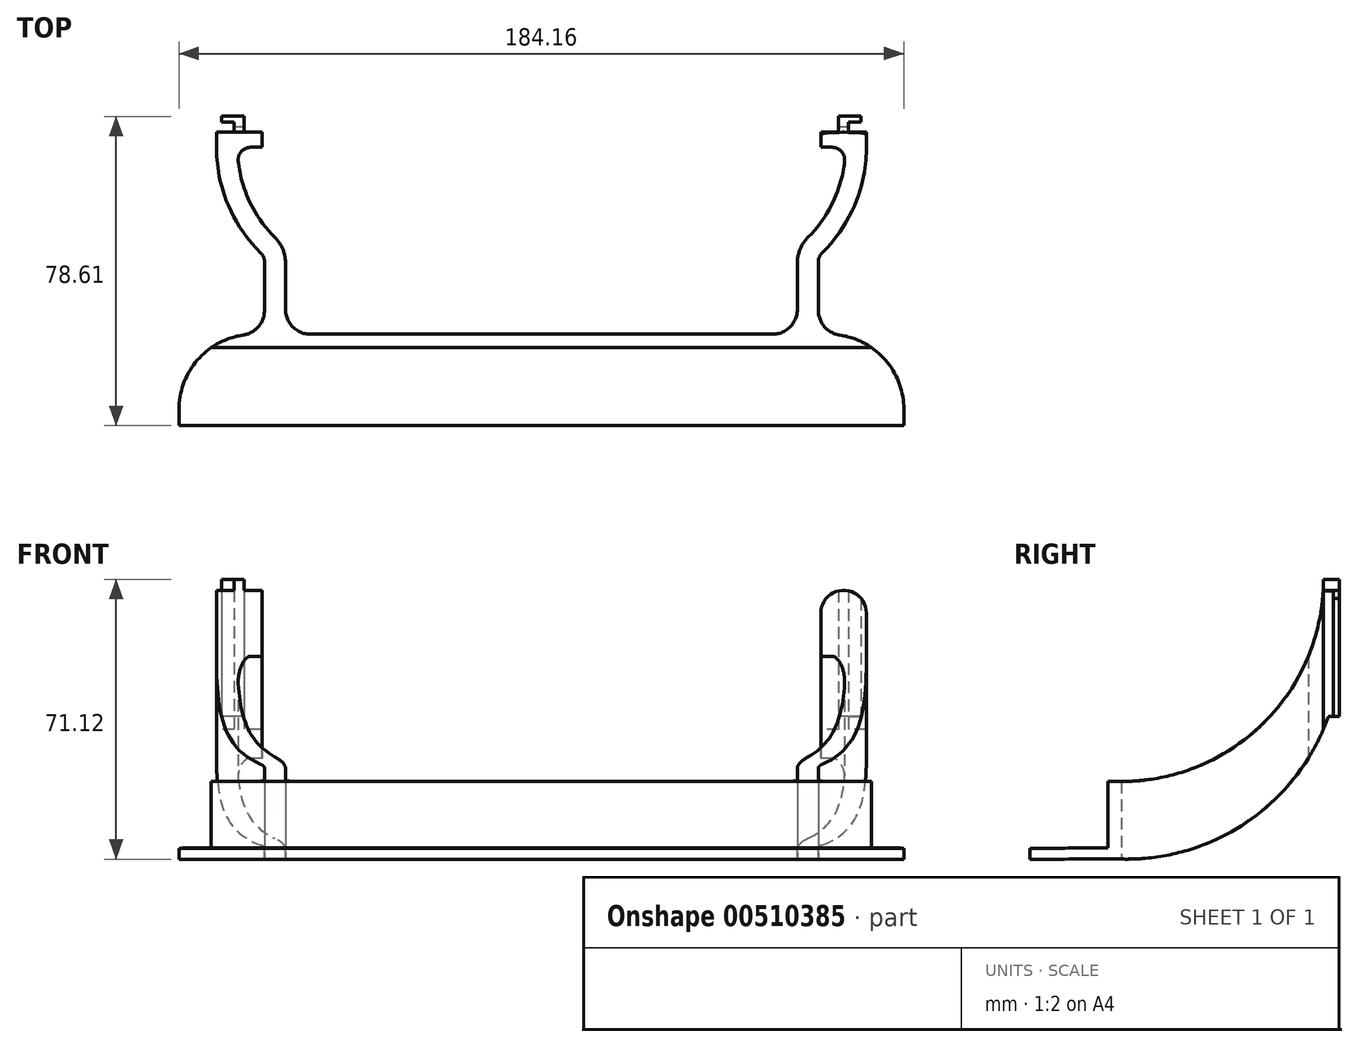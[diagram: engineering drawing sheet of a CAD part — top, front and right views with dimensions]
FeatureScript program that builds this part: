
annotation { "Feature Type Name" : "Feature", "Feature Type Description" : "" }
export const myFeature = defineFeature(function(context is Context, id is Id, definition is map)
    precondition{}
    {
        {
            var Q0;
            Q0=qCreatedBy(makeId("Top.planeOp"),FACE);
            var sketch = newSketch(context, id + "F0", { "sketchPlane" : qUnion([Q0])});
            skLineSegment(sketch, "E0", {"start": v(0, 0) * mm, "end": v(92.07, 0) * mm});
            skLineSegment(sketch, "E1.0", {"start": v(0, 23.24) * mm, "end": v(58.67, 23.24) * mm});
            skLineSegment(sketch, "E2", {"start": v(70.36, 41.66) * mm, "end": v(70.36, 29.32) * mm});
            skLineSegment(sketch, "E3.0", {"start": v(65.02, 41.35) * mm, "end": v(65.02, 29.6) * mm});
            skLineSegment(sketch, "E4", {"start": v(92.07, 0) * mm, "end": v(92.07, 4.2) * mm});
            skPoint(sketch, "E5.visualSharp", {"position": v(92.07, 23.24) * mm});
            skArc(sketch, "E5.filletArc", {"start": v(92.07, 4.2) * mm, "mid": v(87.44, 16.65) * mm, "end": v(75.79, 23.04) * mm});
            skLineSegment(sketch, "E6", {"start": v(82.55, 74.55) * mm, "end": v(82.55, 70.74) * mm});
            skArc(sketch, "E7.trimOffspring", {"start": v(71.3, 43.93) * mm, "mid": v(79.63, 56.2) * mm, "end": v(82.55, 70.74) * mm});
            skArc(sketch, "E8.0", {"start": v(67.75, 47.9) * mm, "mid": v(74.03, 56.77) * mm, "end": v(77.02, 67.22) * mm});
            skLineSegment(sketch, "E9.0", {"start": v(71, 74.55) * mm, "end": v(71, 70.74) * mm});
            skLineSegment(sketch, "E10.trimOffspring", {"start": v(71, 74.55) * mm, "end": v(75.5, 74.55) * mm});
            skLineSegment(sketch, "E11.trimOffspring", {"start": v(71, 70.74) * mm, "end": v(73.87, 70.74) * mm});
            skLineSegment(sketch, "E12", {"start": v(76.77, 74.55) * mm, "end": v(76.77, 78.65) * mm, "construction": true});
            skLineSegment(sketch, "E13.0", {"start": v(78.04, 74.55) * mm, "end": v(78.04, 77.09) * mm});
            skLineSegment(sketch, "E14.0", {"start": v(75.5, 74.55) * mm, "end": v(75.5, 78.65) * mm});
            skLineSegment(sketch, "E15.trimOffspring", {"start": v(78.04, 74.55) * mm, "end": v(82.55, 74.55) * mm});
            skLineSegment(sketch, "E16.0", {"start": v(78.04, 77.09) * mm, "end": v(81.22, 77.09) * mm});
            skLineSegment(sketch, "E17.0", {"start": v(75.5, 78.61) * mm, "end": v(81.22, 78.61) * mm});
            skLineSegment(sketch, "E18.trimOffspring", {"start": v(78.04, 78.61) * mm, "end": v(78.04, 78.65) * mm});
            skLineSegment(sketch, "E19.0", {"start": v(81.22, 77.09) * mm, "end": v(81.22, 78.65) * mm});
            skLineSegment(sketch, "E20.MirrorCS", {"start": v(0, 23.24) * mm, "end": v(-58.67, 23.24) * mm});
            skLineSegment(sketch, "E21.MirrorCS", {"start": v(0, 0) * mm, "end": v(-92.07, 0) * mm});
            skArc(sketch, "E22.MirrorCS", {"start": v(-92.07, 4.2) * mm, "mid": v(-87.44, 16.65) * mm, "end": v(-75.79, 23.04) * mm});
            skLineSegment(sketch, "E23.MirrorCS", {"start": v(-65.02, 41.35) * mm, "end": v(-65.02, 29.6) * mm});
            skLineSegment(sketch, "E24.MirrorCS", {"start": v(-92.07, 0) * mm, "end": v(-92.07, 4.2) * mm});
            skLineSegment(sketch, "E25.MirrorCS", {"start": v(-70.36, 41.66) * mm, "end": v(-70.36, 29.32) * mm});
            skArc(sketch, "E26.MirrorCS", {"start": v(-71.3, 43.93) * mm, "mid": v(-79.63, 56.2) * mm, "end": v(-82.55, 70.74) * mm});
            skArc(sketch, "E27.MirrorCS", {"start": v(-67.75, 47.9) * mm, "mid": v(-74.03, 56.77) * mm, "end": v(-77.02, 67.22) * mm});
            skLineSegment(sketch, "E28.MirrorCS", {"start": v(-71, 70.74) * mm, "end": v(-73.87, 70.74) * mm});
            skLineSegment(sketch, "E29.MirrorCS", {"start": v(-71, 74.55) * mm, "end": v(-71, 70.74) * mm});
            skLineSegment(sketch, "E30.MirrorCS", {"start": v(-71, 74.55) * mm, "end": v(-75.5, 74.55) * mm});
            skLineSegment(sketch, "E31.MirrorCS", {"start": v(-75.5, 74.55) * mm, "end": v(-75.5, 78.65) * mm});
            skLineSegment(sketch, "E32.MirrorCS", {"start": v(-75.5, 78.61) * mm, "end": v(-81.22, 78.61) * mm});
            skLineSegment(sketch, "E33.MirrorCS", {"start": v(-78.04, 77.09) * mm, "end": v(-81.22, 77.09) * mm});
            skLineSegment(sketch, "E34.MirrorCS", {"start": v(-82.55, 74.55) * mm, "end": v(-82.55, 70.74) * mm});
            skLineSegment(sketch, "E35.MirrorCS", {"start": v(-78.04, 74.55) * mm, "end": v(-82.55, 74.55) * mm});
            skLineSegment(sketch, "E36.MirrorCS", {"start": v(-78.04, 74.55) * mm, "end": v(-78.04, 77.09) * mm});
            skLineSegment(sketch, "E37.MirrorCS", {"start": v(-81.22, 77.09) * mm, "end": v(-81.22, 78.65) * mm});
            skPoint(sketch, "E38.visualSharp", {"position": v(65.02, 23.24) * mm});
            skArc(sketch, "E38.filletArc", {"start": v(58.67, 23.24) * mm, "mid": v(63.16, 25.1) * mm, "end": v(65.02, 29.6) * mm});
            skPoint(sketch, "E39.newPointA", {"position": v(73.02, 23.24) * mm});
            skPoint(sketch, "E39.newPointB", {"position": v(70.36, 23.24) * mm});
            skArc(sketch, "E39.filletArc", {"start": v(70.36, 29.32) * mm, "mid": v(71.9, 25.17) * mm, "end": v(75.79, 23.04) * mm});
            skPoint(sketch, "E40.visualSharp", {"position": v(-65.02, 23.24) * mm});
            skArc(sketch, "E40.filletArc", {"start": v(-65.02, 29.6) * mm, "mid": v(-63.16, 25.1) * mm, "end": v(-58.67, 23.24) * mm});
            skArc(sketch, "E41.filletArc", {"start": v(-75.79, 23.04) * mm, "mid": v(-71.9, 25.17) * mm, "end": v(-70.36, 29.32) * mm});
            skPoint(sketch, "E42.visualSharp", {"position": v(-77.22, 70.74) * mm});
            skArc(sketch, "E42.filletArc", {"start": v(-73.87, 70.74) * mm, "mid": v(-76.23, 69.68) * mm, "end": v(-77.02, 67.22) * mm});
            skPoint(sketch, "E43.visualSharp", {"position": v(77.22, 70.74) * mm});
            skArc(sketch, "E43.filletArc", {"start": v(77.02, 67.22) * mm, "mid": v(76.23, 69.68) * mm, "end": v(73.87, 70.74) * mm});
            skPoint(sketch, "E44.visualSharp", {"position": v(-70.36, 43.03) * mm});
            skArc(sketch, "E44.filletArc", {"start": v(-70.36, 41.66) * mm, "mid": v(-70.6, 42.9) * mm, "end": v(-71.3, 43.93) * mm});
            skPoint(sketch, "E45.visualSharp", {"position": v(-65.02, 45.48) * mm});
            skArc(sketch, "E45.filletArc", {"start": v(-65.02, 41.35) * mm, "mid": v(-65.73, 44.9) * mm, "end": v(-67.75, 47.9) * mm});
            skPoint(sketch, "E46.visualSharp", {"position": v(65.02, 45.48) * mm});
            skArc(sketch, "E46.filletArc", {"start": v(67.75, 47.9) * mm, "mid": v(65.73, 44.9) * mm, "end": v(65.02, 41.35) * mm});
            skPoint(sketch, "E47.visualSharp", {"position": v(70.36, 43.03) * mm});
            skArc(sketch, "E47.filletArc", {"start": v(71.3, 43.93) * mm, "mid": v(70.6, 42.9) * mm, "end": v(70.36, 41.66) * mm});
            skSolve(sketch);
        }
        {
            var Q0;
            Q0=makeQuery(id+"F0.imprint","IMPRINT",FACE,{"disambiguationData":[TD([[makeQuery(id+"F0.imprint","IMPRINT",EDGE,{"derivedFrom":sQuery(id+"F0.wireOp",EDGE,"E0")}),1.0]])]});
            extrude(context, id + "F1", {"entities" : qUnion([Q0]), "depth" : 71.12 * mm});
        }
        {
            var Q0;
            Q0=qCreatedBy(makeId("Right.planeOp"),FACE);
            var sketch = newSketch(context, id + "F2", { "sketchPlane" : qUnion([Q0])});
            skLineSegment(sketch, "E48.0.0", {"start": v(4.85, 0.47) * mm, "end": v(23.24, 0.02) * mm});
            skLineSegment(sketch, "E49", {"start": v(0, 0) * mm, "end": v(23.24, 0.02) * mm});
            skLineSegment(sketch, "E50.0", {"start": v(0.05, 2.8) * mm, "end": v(19.86, 2.81) * mm});
            skLineSegment(sketch, "E51", {"start": v(0, 0) * mm, "end": v(0.05, 2.8) * mm});
            skLineSegment(sketch, "E52.0", {"start": v(19.86, 2.81) * mm, "end": v(19.86, 19.74) * mm});
            skLineSegment(sketch, "E53.trimOffspring", {"start": v(19.86, 19.74) * mm, "end": v(23.24, 19.74) * mm});
            skLineSegment(sketch, "E54", {"start": v(75.87, 36.32) * mm, "end": v(78.61, 36.32) * mm});
            skArc(sketch, "E55", {"start": v(23.24, 0.02) * mm, "mid": v(55.45, 9.63) * mm, "end": v(75.87, 36.32) * mm});
            skLineSegment(sketch, "E56.0", {"start": v(78.61, 71.12) * mm, "end": v(78.61, 36.32) * mm});
            skLineSegment(sketch, "E57", {"start": v(78.61, 36.32) * mm, "end": v(78.61, 71.12) * mm});
            skPoint(sketch, "E58.orphan", {"position": v(78.61, -71.02) * mm});
            skLineSegment(sketch, "E59", {"start": v(78.61, 71.12) * mm, "end": v(74.63, 71.12) * mm});
            skPoint(sketch, "E60.orphan", {"position": v(23.24, 71.12) * mm});
            skLineSegment(sketch, "E61", {"start": v(74.63, 71.12) * mm, "end": v(15.79, 71.12) * mm, "construction": true});
            skLineSegment(sketch, "E62", {"start": v(23.24, 19.74) * mm, "end": v(23.24, 79.24) * mm, "construction": true});
            skArc(sketch, "E63", {"start": v(23.24, 19.74) * mm, "mid": v(59.58, 34.79) * mm, "end": v(74.63, 71.12) * mm});
            skLineSegment(sketch, "E64.filletArc", {"start": v(74.63, 71.12) * mm, "end": v(74.63, 71.12) * mm});
            skSolve(sketch);
        }
        {
            var Q0;
            Q0 = qSketchRegion(id + "F2", true);
            extrude(context, id + "F3", {"entities" : qUnion([Q0]), "operationType" : NewBodyOperationType.INTERSECT, "endBound" : BoundingType.SYMMETRIC, "depth" : 203.2 * mm});
        }
        {
            var Q0;
            Q0=qCreatedBy(makeId("Front.planeOp"),FACE);
            var sketch = newSketch(context, id + "F4", { "sketchPlane" : qUnion([Q0])});
            skLineSegment(sketch, "E65.0", {"start": v(78.04, 71.12) * mm, "end": v(75.5, 71.12) * mm});
            skLineSegment(sketch, "E66", {"start": v(76.77, 71.12) * mm, "end": v(76.77, 54.7) * mm, "construction": true});
            skLineSegment(sketch, "E67.0", {"start": v(71, 68.32) * mm, "end": v(71, 51.52) * mm});
            skLineSegment(sketch, "E68.0", {"start": v(82.55, 68.32) * mm, "end": v(82.55, 51.52) * mm});
            skLineSegment(sketch, "E69.0", {"start": v(78.04, 68.32) * mm, "end": v(82.55, 68.32) * mm});
            skLineSegment(sketch, "E70.0", {"start": v(76.77, 62.54) * mm, "end": v(82.55, 62.54) * mm});
            skArc(sketch, "E71", {"start": v(82.55, 62.54) * mm, "mid": v(76.77, 68.32) * mm, "end": v(71, 62.54) * mm});
            skLineSegment(sketch, "E72", {"start": v(82.55, 62.54) * mm, "end": v(85.77, 62.54) * mm});
            skLineSegment(sketch, "E73", {"start": v(85.77, 62.54) * mm, "end": v(85.77, 73.42) * mm});
            skLineSegment(sketch, "E74", {"start": v(85.77, 73.42) * mm, "end": v(67.02, 73.42) * mm});
            skLineSegment(sketch, "E75", {"start": v(67.02, 73.42) * mm, "end": v(67.02, 62.54) * mm});
            skLineSegment(sketch, "E76", {"start": v(67.02, 62.54) * mm, "end": v(71, 62.54) * mm});
            skArc(sketch, "E77.MirrorCS", {"start": v(-82.55, 62.54) * mm, "mid": v(-76.77, 68.32) * mm, "end": v(-71, 62.54) * mm});
            skLineSegment(sketch, "E78.MirrorCS", {"start": v(-67.02, 62.54) * mm, "end": v(-71, 62.54) * mm});
            skLineSegment(sketch, "E79.MirrorCS", {"start": v(-67.02, 73.42) * mm, "end": v(-67.02, 62.54) * mm});
            skLineSegment(sketch, "E80.MirrorCS", {"start": v(-85.77, 73.42) * mm, "end": v(-67.02, 73.42) * mm});
            skLineSegment(sketch, "E81.MirrorCS", {"start": v(-85.77, 62.54) * mm, "end": v(-85.77, 73.42) * mm});
            skLineSegment(sketch, "E82.MirrorCS", {"start": v(-82.55, 62.54) * mm, "end": v(-85.77, 62.54) * mm});
            skSolve(sketch);
        }
        {
            var Q0;
            Q0=makeQuery(id+"F4.imprint","IMPRINT",FACE,{"disambiguationData":[TD([[makeQuery(id+"F4.imprint","IMPRINT",EDGE,{"derivedFrom":sQuery(id+"F4.wireOp",EDGE,"E77.MirrorCS")}),1.0]])]});
            var Q1;
            Q1=makeQuery(id+"F4.imprint","IMPRINT",FACE,{"disambiguationData":[TD([[makeQuery(id+"F4.imprint","IMPRINT",EDGE,{"derivedFrom":sQuery(id+"F4.wireOp",EDGE,"E71")}),-1.0]])]});
            extrude(context, id + "F5", {"entities" : qUnion([Q0, Q1]), "operationType" : NewBodyOperationType.REMOVE, "endBound" : BoundingType.THROUGH_ALL, "oppositeDirection" : true, "depth" : 25.4 * mm});
        }
    });
